# Revit family: Cabinet-Teknion-CEUPL_Upper_Cabinet_Pigeonholes-R2022
name_source: partatom
category: Furniture
units: mm (PartAtom-declared; Revit-internal decimal feet)

## family parameters
Always vertical = Yes
Cut with Voids When Loaded = No
Enable Cutting in Views = No
OmniClass Number = 23.40.20.00
OmniClass Title = General Furniture and Specialties
Render Appearance Source = Family Geometry
Room Calculation Point = No
Shared = Yes
Work Plane-Based = No

## types (4) — shared parameters
Assembly Code = E2020200
Manufacturer = Teknion
Manufacturer Fax = 416.661.4586
Part Number = CEUPL
Product Documentation Link = https://www.teknion.com
Product Line = Upper Cabinets
Product Page URL = https://www.teknion.com
Series = Expansion Casework+
Sustainability Data = https://www.teknion.com
URL = www.teknion.com
Unit Weight URL = http://www.teknion.com
Warranty = http://www.teknion.com
zero-valued in all types: Default Elevation

## per-type parameters (varying)
| type | Description | Height | Model |
| Height 36 | Upper Cabinet – Pigeonholes,15"D,36"H | 36 " | CEUPL15_36 |
| Height 33 | Upper Cabinet – Pigeonholes,15"D,33"H | 33 " | CEUPL15_33 |
| Height 30 | Upper Cabinet – Pigeonholes,15"D,30"H | 30 " | CEUPL15_30 |
| Height 27 | Upper Cabinet – Pigeonholes,15"D,27"H | 27 " | CEUPL15_27 |

## geometry (parser evidence)
native form markers: Sweep x3
no freeform markers — native parametric forms only
